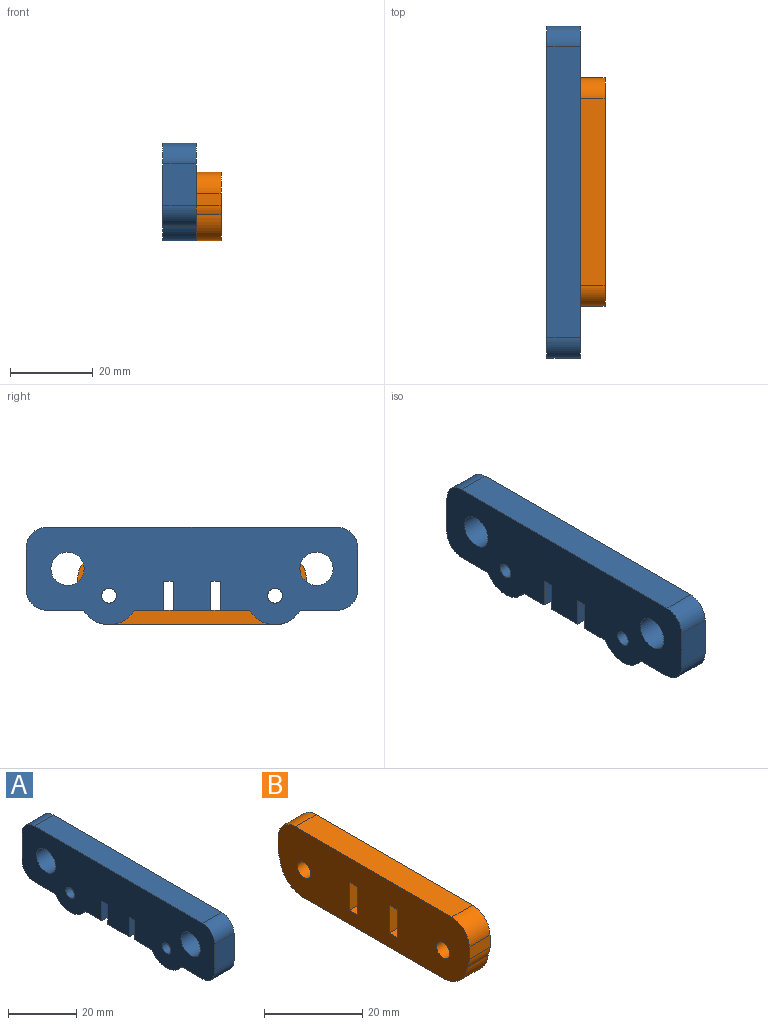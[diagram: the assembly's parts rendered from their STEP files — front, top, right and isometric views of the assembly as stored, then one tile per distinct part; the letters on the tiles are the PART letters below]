
ASSEMBLY  parts=2 mates=1
PART A: 40 faces, bbox 8x80x23.5 mm
  f0: cylinder r=1.8mm len=5mm, axis (-1,0,0), area 56.5mm2, adj f25,f39
  f1: cylinder r=1.8mm len=5mm, axis (-1,0,0), area 56.5mm2, adj f25,f32
  f2: plane 80x23.5mm, normal (1,0,0), area 1450.3mm2, adj f3,f4,f5,f6,f7,f8,f9,f10
  f3: plane 8x2.4mm, normal (0,0,-1), area 19.2mm2, adj f2,f4,f24,f25
  f4: plane 8x7mm, normal (0,-1,0), area 56mm2, adj f2,f3,f5,f25
  f5: plane 8x7.04mm, normal (0,0,-1), area 56.3mm2, adj f2,f4,f6,f25
  f6: cylinder r=7mm len=12.12mm, axis (-1,0,0), area 117.3mm2, adj f2,f5,f7,f25
  f7: plane 8.94x8mm, normal (0,0,-1), area 71.5mm2, adj f2,f6,f8,f25
  f8: cylinder r=5mm len=8mm, axis (-1,0,0), area 62.8mm2, adj f2,f7,f9,f25
  f9: plane 10x8mm, normal (0,1,0), area 80mm2, adj f2,f8,f10,f25
  f10: cylinder r=5mm len=8mm, axis (-1,0,0), area 62.8mm2, adj f2,f9,f11,f25
  f11: plane 70x8mm, normal (0,0,1), area 560mm2, adj f2,f10,f12,f25
  f12: cylinder r=5mm len=8mm, axis (-1,0,0), area 62.8mm2, adj f2,f11,f13,f25
  f13: plane 10x8mm, normal (0,-1,0), area 80mm2, adj f2,f12,f14,f25
  f14: cylinder r=5mm len=8mm, axis (-1,0,0), area 62.8mm2, adj f2,f13,f15,f25
  f15: plane 8.94x8mm, normal (0,0,-1), area 71.5mm2, adj f2,f14,f16,f25
  f16: cylinder r=7mm len=12.12mm, axis (-1,0,0), area 117.3mm2, adj f2,f15,f17,f25
  f17: plane 8x7.04mm, normal (0,0,-1), area 56.3mm2, adj f2,f16,f18,f25
  f18: plane 8x7mm, normal (0,1,0), area 56mm2, adj f2,f17,f19,f25
  f19: plane 8x2.4mm, normal (0,0,-1), area 19.2mm2, adj f2,f18,f20,f25
  f20: plane 8x7mm, normal (0,-1,0), area 56mm2, adj f2,f19,f21,f25
  f21: plane 9x8mm, normal (0,0,-1), area 72mm2, adj f2,f20,f24,f25
  f22: cylinder r=4mm len=8mm, axis (-1,0,0), area 201.1mm2, adj f2,f25
  f23: cylinder r=4mm len=8mm, axis (-1,0,0), area 201.1mm2, adj f2,f25
  f24: plane 8x7mm, normal (0,1,0), area 56mm2, adj f2,f3,f21,f25
  f25: plane 80x23.5mm, normal (-1,0,0), area 1484.2mm2, adj f0,f1,f3,f4,f5,f6,f7,f8
  f26: plane 3x2.8mm, normal (0,0.87,-0.5), area 9.7mm2, adj f2,f27,f31,f32
  f27: plane 3x2.8mm, normal (0,0.87,0.5), area 9.7mm2, adj f2,f26,f28,f32
  f28: plane 3.23x3mm, normal (0,0,1), area 9.7mm2, adj f2,f27,f29,f32
  f29: plane 3x2.8mm, normal (0,-0.87,0.5), area 9.7mm2, adj f2,f28,f30,f32
  f30: plane 3x2.8mm, normal (0,-0.87,-0.5), area 9.7mm2, adj f2,f29,f31,f32
  f31: plane 3.23x3mm, normal (0,0,-1), area 9.7mm2, adj f2,f26,f30,f32
  f32: plane 6.47x5.6mm, normal (1,0,0), area 17mm2, adj f1,f26,f27,f28,f29,f30,f31
  f33: plane 3x2.8mm, normal (0,0.87,-0.5), area 9.7mm2, adj f2,f34,f38,f39
  f34: plane 3x2.8mm, normal (0,0.87,0.5), area 9.7mm2, adj f2,f33,f35,f39
  f35: plane 3.23x3mm, normal (0,0,1), area 9.7mm2, adj f2,f34,f36,f39
  f36: plane 3x2.8mm, normal (0,-0.87,0.5), area 9.7mm2, adj f2,f35,f37,f39
  f37: plane 3x2.8mm, normal (0,-0.87,-0.5), area 9.7mm2, adj f2,f36,f38,f39
  f38: plane 3.23x3mm, normal (0,0,-1), area 9.7mm2, adj f2,f33,f37,f39
  f39: plane 6.47x5.6mm, normal (1,0,0), area 17mm2, adj f0,f33,f34,f35,f36,f37,f38
PART B: 22 faces, bbox 6x55x16.5 mm
  f0: plane 6x2.4mm, normal (0,0,1), area 14.4mm2, adj f1,f16,f20,f21
  f1: plane 7x6mm, normal (0,1,0), area 42mm2, adj f0,f2,f20,f21
  f2: plane 6x2.4mm, normal (0,0,-1), area 14.4mm2, adj f1,f16,f20,f21
  f3: plane 6x2.4mm, normal (0,0,1), area 14.4mm2, adj f4,f17,f20,f21
  f4: plane 7x6mm, normal (0,1,0), area 42mm2, adj f3,f5,f20,f21
  f5: plane 6x2.4mm, normal (0,0,-1), area 14.4mm2, adj f4,f17,f20,f21
  f6: cylinder r=7mm len=6.87mm, axis (-1,0,0), area 60.9mm2, adj f7,f18,f20,f21
  f7: plane 40.09x6mm, normal (0,0,-1), area 240.5mm2, adj f6,f8,f20,f21
  f8: cylinder r=7mm len=6.96mm, axis (-1,0,0), area 61.4mm2, adj f7,f9,f20,f21
  f9: cylinder r=5mm len=6mm, axis (-1,0,0), area 14.1mm2, adj f8,f10,f20,f21
  f10: plane 6x3mm, normal (0,1,0), area 18mm2, adj f9,f11,f20,f21
  f11: cylinder r=5mm len=6mm, axis (-1,0,0), area 47.1mm2, adj f10,f12,f20,f21
  f12: plane 45x6mm, normal (0,0,1), area 270mm2, adj f11,f13,f20,f21
  f13: cylinder r=5mm len=6mm, axis (-1,0,0), area 47.1mm2, adj f12,f14,f20,f21
  f14: plane 6x3mm, normal (0,-1,0), area 18mm2, adj f13,f18,f20,f21
  f15: cylinder r=1.9mm len=6mm, axis (-1,0,0), area 71.6mm2, adj f20,f21
  f16: plane 7x6mm, normal (0,-1,0), area 42mm2, adj f0,f2,f20,f21
  f17: plane 7x6mm, normal (0,-1,0), area 42mm2, adj f3,f5,f20,f21
  f18: cylinder r=5mm len=6mm, axis (-1,0,0), area 14.1mm2, adj f6,f14,f20,f21
  f19: cylinder r=1.9mm len=6mm, axis (-1,0,0), area 71.6mm2, adj f20,f21
  f20: plane 55x16.5mm, normal (1,0,0), area 812.4mm2, adj f0,f1,f2,f3,f4,f5,f6,f7
  f21: plane 55x16.5mm, normal (-1,0,0), area 812.4mm2, adj f0,f1,f2,f3,f4,f5,f6,f7
PLACE A t=(-34.78,15.1,-17.42)mm
PLACE B t=(-30.78,15.1,49.27)mm
MATE fastened B.f21 <-> A.f2  axis (-1,0,0) through (-30.78,8.2,42.77)mm
